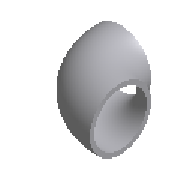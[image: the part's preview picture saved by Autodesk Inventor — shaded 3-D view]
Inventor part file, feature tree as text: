
AUTODESK INVENTOR PART (.ipt)
format: ipt  version: 2023.2 (Build 272271030, 271C)  size: 188,928 bytes
history: native  units: mm (DEFAULTED — no unit token found)
features: other x4, sketch x2, sweep x1
ambient origin geometry x8: Origin, YZ Plane, XZ Plane, XY Plane, X Axis, Y Axis, Z Axis, Center Point
bodies: Solid1 (feature_tree)
feature tree (7):
  sweep  "Sweep1"
  other  "Work Point1"
  other  "Work Point2"
  other  "Work Axis1"
  other  "Work Axis2"
  sketch  "Sketch1"  dims[d0=56.3mm d1=60.3mm]
  sketch  "Sketch2"  dims[d2=51.0mm d3=51.0mm d4=0.0mm d5=0.0mm]
